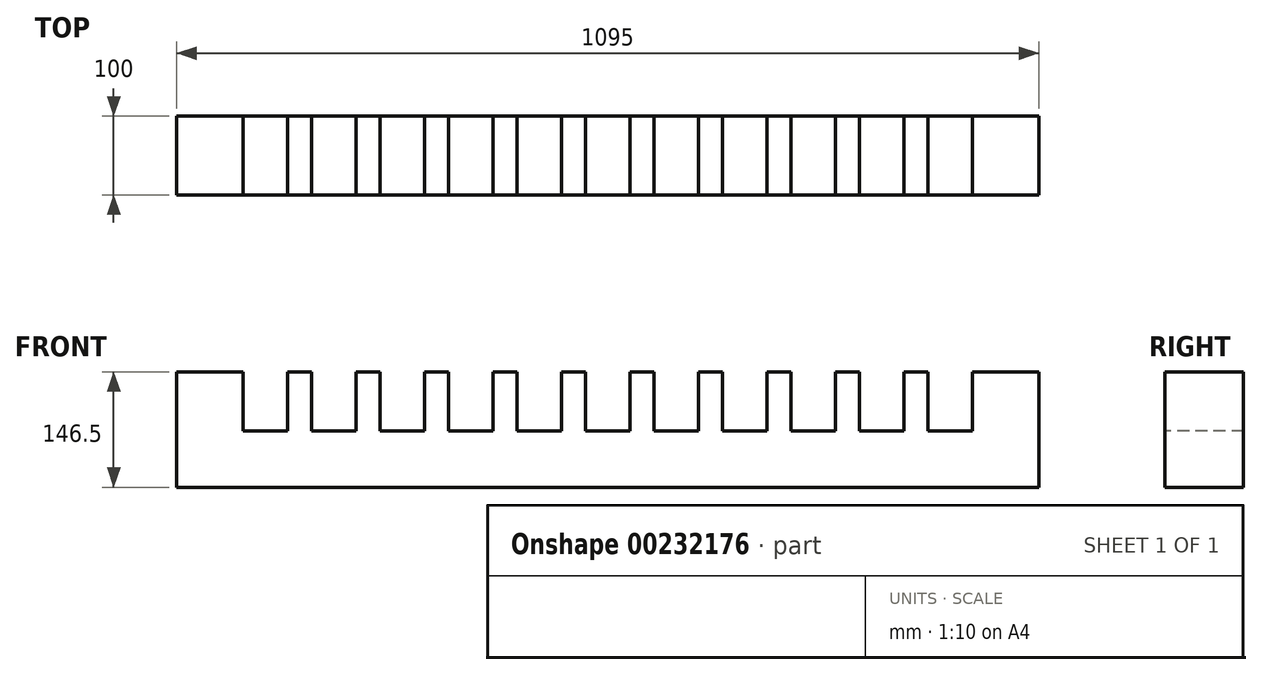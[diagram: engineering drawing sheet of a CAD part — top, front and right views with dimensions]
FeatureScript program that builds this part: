
annotation { "Feature Type Name" : "Feature", "Feature Type Description" : "" }
export const myFeature = defineFeature(function(context is Context, id is Id, definition is map)
    precondition{}
    {
        {
            var Q0;
            Q0=qCreatedBy(makeId("Right.planeOp"),FACE);
            var sketch = newSketch(context, id + "F0", { "sketchPlane" : qUnion([Q0])});
            skLineSegment(sketch, "E0.bottom", {"start": v(-50, 108.54) * mm, "end": v(50, 108.54) * mm});
            skLineSegment(sketch, "E0.top", {"start": v(-50, -37.96) * mm, "end": v(50, -37.96) * mm});
            skLineSegment(sketch, "E0.left", {"start": v(-50, 108.54) * mm, "end": v(-50, -37.96) * mm});
            skLineSegment(sketch, "E0.right", {"start": v(50, 108.54) * mm, "end": v(50, -37.96) * mm});
            skSolve(sketch);
        }
        {
            var Q0;
            Q0=makeQuery(id+"F0.imprint","IMPRINT",FACE,{"disambiguationData":[TD([[makeQuery(id+"F0.imprint","IMPRINT",EDGE,{"derivedFrom":sQuery(id+"F0.wireOp",EDGE,"E0.bottom")}),-1.0]])]});
            extrude(context, id + "F1", {"entities" : qUnion([Q0]), "depth" : 1095 * mm});
        }
        {
            var Q0;
            Q0=makeQuery(id+"F1.opExtrude","SWEPT_FACE",FACE,{"disambiguationData":[OSD([sQuery(id+"F0.wireOp",EDGE,"E0.left")])]});
            var sketch = newSketch(context, id + "F2", { "sketchPlane" : qUnion([Q0])});
            skLineSegment(sketch, "E1.bottom", {"start": v(84, 108.54) * mm, "end": v(141, 108.54) * mm});
            skLineSegment(sketch, "E1.top", {"start": v(84, 33.54) * mm, "end": v(141, 33.54) * mm});
            skLineSegment(sketch, "E1.left", {"start": v(84, 108.54) * mm, "end": v(84, 33.54) * mm});
            skLineSegment(sketch, "E1.right", {"start": v(141, 108.54) * mm, "end": v(141, 33.54) * mm});
            skLineSegment(sketch, "E2.bottom", {"start": v(171, 108.54) * mm, "end": v(228, 108.54) * mm});
            skLineSegment(sketch, "E2.top", {"start": v(171, 33.54) * mm, "end": v(228, 33.54) * mm});
            skLineSegment(sketch, "E2.left", {"start": v(171, 108.54) * mm, "end": v(171, 33.54) * mm});
            skLineSegment(sketch, "E2.right", {"start": v(228, 108.54) * mm, "end": v(228, 33.54) * mm});
            skLineSegment(sketch, "E3.bottom", {"start": v(258, 108.54) * mm, "end": v(315, 108.54) * mm});
            skLineSegment(sketch, "E3.top", {"start": v(258, 33.54) * mm, "end": v(315, 33.54) * mm});
            skLineSegment(sketch, "E3.left", {"start": v(258, 108.54) * mm, "end": v(258, 33.54) * mm});
            skLineSegment(sketch, "E3.right", {"start": v(315, 108.54) * mm, "end": v(315, 33.54) * mm});
            skLineSegment(sketch, "E4.bottom", {"start": v(345, 108.54) * mm, "end": v(402, 108.54) * mm});
            skLineSegment(sketch, "E4.top", {"start": v(345, 33.54) * mm, "end": v(402, 33.54) * mm});
            skLineSegment(sketch, "E4.left", {"start": v(345, 108.54) * mm, "end": v(345, 33.54) * mm});
            skLineSegment(sketch, "E4.right", {"start": v(402, 108.54) * mm, "end": v(402, 33.54) * mm});
            skLineSegment(sketch, "E5.bottom", {"start": v(432, 108.54) * mm, "end": v(489, 108.54) * mm});
            skLineSegment(sketch, "E5.top", {"start": v(432, 33.54) * mm, "end": v(489, 33.54) * mm});
            skLineSegment(sketch, "E5.left", {"start": v(432, 108.54) * mm, "end": v(432, 33.54) * mm});
            skLineSegment(sketch, "E5.right", {"start": v(489, 108.54) * mm, "end": v(489, 33.54) * mm});
            skLineSegment(sketch, "E6.bottom", {"start": v(519, 108.54) * mm, "end": v(576, 108.54) * mm});
            skLineSegment(sketch, "E6.top", {"start": v(519, 33.54) * mm, "end": v(576, 33.54) * mm});
            skLineSegment(sketch, "E6.left", {"start": v(519, 108.54) * mm, "end": v(519, 33.54) * mm});
            skLineSegment(sketch, "E6.right", {"start": v(576, 108.54) * mm, "end": v(576, 33.54) * mm});
            skLineSegment(sketch, "E7.bottom", {"start": v(606, 108.54) * mm, "end": v(663, 108.54) * mm});
            skLineSegment(sketch, "E7.top", {"start": v(606, 33.54) * mm, "end": v(663, 33.54) * mm});
            skLineSegment(sketch, "E7.left", {"start": v(606, 108.54) * mm, "end": v(606, 33.54) * mm});
            skLineSegment(sketch, "E7.right", {"start": v(663, 108.54) * mm, "end": v(663, 33.54) * mm});
            skLineSegment(sketch, "E8.bottom", {"start": v(693, 108.54) * mm, "end": v(750, 108.54) * mm});
            skLineSegment(sketch, "E8.top", {"start": v(693, 33.54) * mm, "end": v(750, 33.54) * mm});
            skLineSegment(sketch, "E8.left", {"start": v(693, 108.54) * mm, "end": v(693, 33.54) * mm});
            skLineSegment(sketch, "E8.right", {"start": v(750, 108.54) * mm, "end": v(750, 33.54) * mm});
            skLineSegment(sketch, "E9.bottom", {"start": v(780, 108.54) * mm, "end": v(837, 108.54) * mm});
            skLineSegment(sketch, "E9.top", {"start": v(780, 33.54) * mm, "end": v(837, 33.54) * mm});
            skLineSegment(sketch, "E9.left", {"start": v(780, 108.54) * mm, "end": v(780, 33.54) * mm});
            skLineSegment(sketch, "E9.right", {"start": v(837, 108.54) * mm, "end": v(837, 33.54) * mm});
            skLineSegment(sketch, "E10.bottom", {"start": v(867, 108.54) * mm, "end": v(924, 108.54) * mm});
            skLineSegment(sketch, "E10.top", {"start": v(867, 33.54) * mm, "end": v(924, 33.54) * mm});
            skLineSegment(sketch, "E10.left", {"start": v(867, 108.54) * mm, "end": v(867, 33.54) * mm});
            skLineSegment(sketch, "E10.right", {"start": v(924, 108.54) * mm, "end": v(924, 33.54) * mm});
            skLineSegment(sketch, "E11.bottom", {"start": v(954, 108.54) * mm, "end": v(1011, 108.54) * mm});
            skLineSegment(sketch, "E11.top", {"start": v(954, 33.54) * mm, "end": v(1011, 33.54) * mm});
            skLineSegment(sketch, "E11.left", {"start": v(954, 108.54) * mm, "end": v(954, 33.54) * mm});
            skLineSegment(sketch, "E11.right", {"start": v(1011, 108.54) * mm, "end": v(1011, 33.54) * mm});
            skSolve(sketch);
        }
        {
            var Q0;
            Q0=makeQuery(id+"F2.imprint","IMPRINT",FACE,{"disambiguationData":[TD([[makeQuery(id+"F2.imprint","IMPRINT",EDGE,{"derivedFrom":sQuery(id+"F2.wireOp",EDGE,"E1.bottom")}),1.0]])]});
            var Q1;
            Q1=makeQuery(id+"F2.imprint","IMPRINT",FACE,{"disambiguationData":[TD([[makeQuery(id+"F2.imprint","IMPRINT",EDGE,{"derivedFrom":sQuery(id+"F2.wireOp",EDGE,"E2.bottom")}),1.0]])]});
            var Q2;
            Q2=makeQuery(id+"F2.imprint","IMPRINT",FACE,{"disambiguationData":[TD([[makeQuery(id+"F2.imprint","IMPRINT",EDGE,{"derivedFrom":sQuery(id+"F2.wireOp",EDGE,"E3.bottom")}),1.0]])]});
            var Q3;
            Q3=makeQuery(id+"F2.imprint","IMPRINT",FACE,{"disambiguationData":[TD([[makeQuery(id+"F2.imprint","IMPRINT",EDGE,{"derivedFrom":sQuery(id+"F2.wireOp",EDGE,"E4.bottom")}),1.0]])]});
            var Q4;
            Q4=makeQuery(id+"F2.imprint","IMPRINT",FACE,{"disambiguationData":[TD([[makeQuery(id+"F2.imprint","IMPRINT",EDGE,{"derivedFrom":sQuery(id+"F2.wireOp",EDGE,"E5.bottom")}),1.0]])]});
            var Q5;
            Q5=makeQuery(id+"F2.imprint","IMPRINT",FACE,{"disambiguationData":[TD([[makeQuery(id+"F2.imprint","IMPRINT",EDGE,{"derivedFrom":sQuery(id+"F2.wireOp",EDGE,"E6.bottom")}),1.0]])]});
            var Q6;
            Q6=makeQuery(id+"F2.imprint","IMPRINT",FACE,{"disambiguationData":[TD([[makeQuery(id+"F2.imprint","IMPRINT",EDGE,{"derivedFrom":sQuery(id+"F2.wireOp",EDGE,"E7.bottom")}),1.0]])]});
            var Q7;
            Q7=makeQuery(id+"F2.imprint","IMPRINT",FACE,{"disambiguationData":[TD([[makeQuery(id+"F2.imprint","IMPRINT",EDGE,{"derivedFrom":sQuery(id+"F2.wireOp",EDGE,"E8.bottom")}),1.0]])]});
            var Q8;
            Q8=makeQuery(id+"F2.imprint","IMPRINT",FACE,{"disambiguationData":[TD([[makeQuery(id+"F2.imprint","IMPRINT",EDGE,{"derivedFrom":sQuery(id+"F2.wireOp",EDGE,"E9.bottom")}),1.0]])]});
            var Q9;
            Q9=makeQuery(id+"F2.imprint","IMPRINT",FACE,{"disambiguationData":[TD([[makeQuery(id+"F2.imprint","IMPRINT",EDGE,{"derivedFrom":sQuery(id+"F2.wireOp",EDGE,"E10.bottom")}),1.0]])]});
            var Q10;
            Q10=makeQuery(id+"F2.imprint","IMPRINT",FACE,{"disambiguationData":[TD([[makeQuery(id+"F2.imprint","IMPRINT",EDGE,{"derivedFrom":sQuery(id+"F2.wireOp",EDGE,"E11.bottom")}),1.0]])]});
            extrude(context, id + "F3", {"entities" : qUnion([Q0, Q1, Q2, Q3, Q4, Q5, Q6, Q7, Q8, Q9, Q10]), "operationType" : NewBodyOperationType.REMOVE, "endBound" : BoundingType.UP_TO_NEXT, "oppositeDirection" : true, "depth" : 25 * mm});
        }
    });
